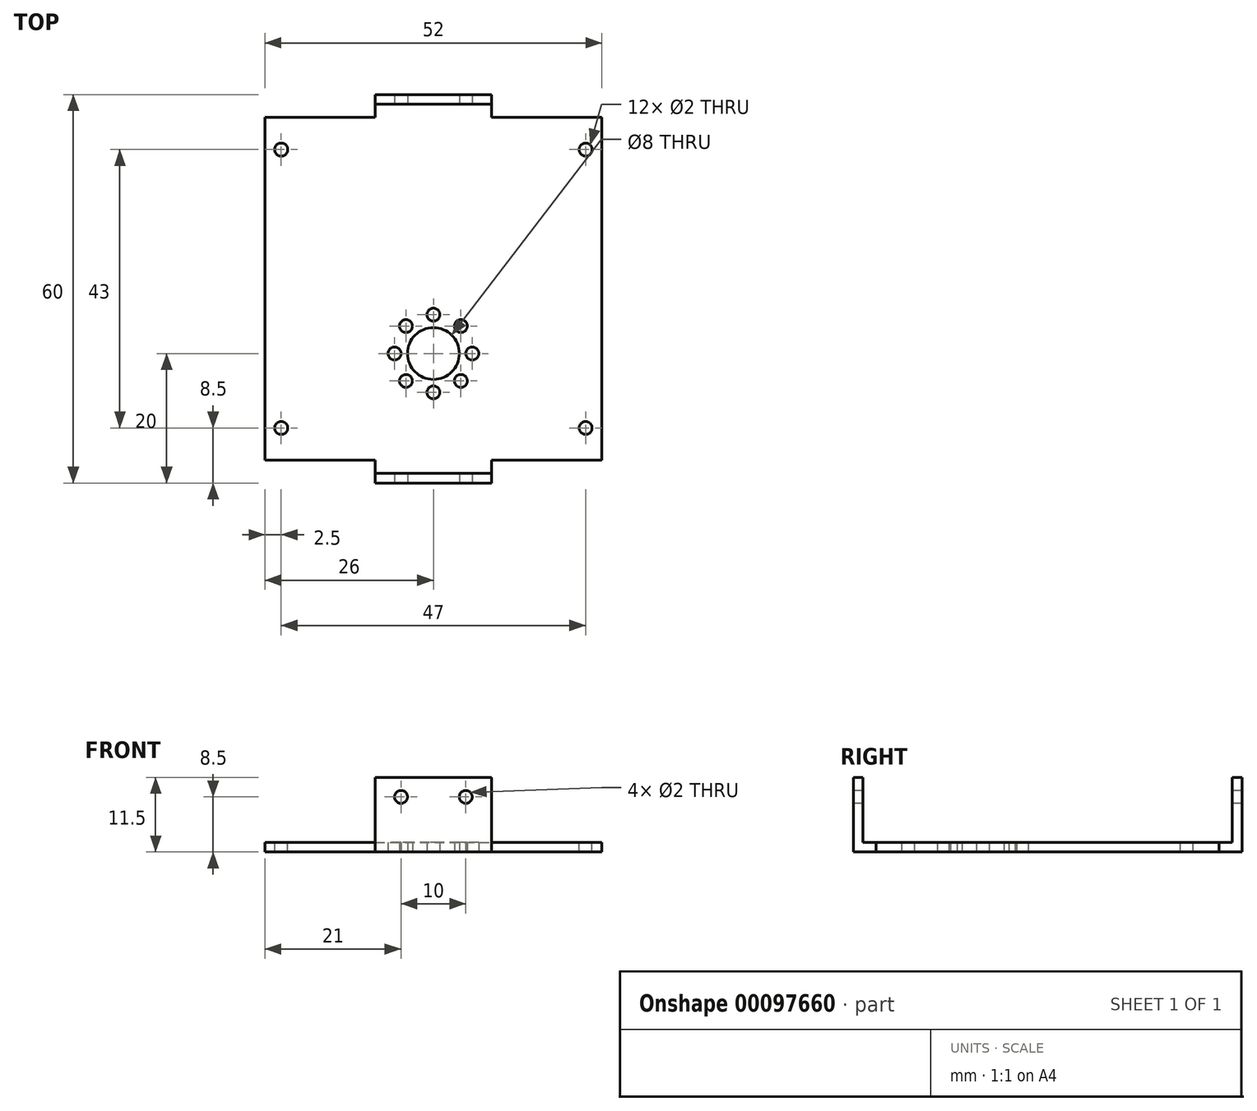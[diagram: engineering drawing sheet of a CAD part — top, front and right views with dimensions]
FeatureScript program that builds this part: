
annotation { "Feature Type Name" : "Feature", "Feature Type Description" : "" }
export const myFeature = defineFeature(function(context is Context, id is Id, definition is map)
    precondition{}
    {
        {
            var Q0;
            Q0=qCreatedBy(makeId("Top.planeOp"),FACE);
            var sketch = newSketch(context, id + "F0", { "sketchPlane" : qUnion([Q0])});
            skCircle(sketch, "E0", {"center": v(0, 0) * mm, "radius": 4 * mm});
            skCircle(sketch, "E1", {"center": v(0, 6) * mm, "radius": 1 * mm});
            skCircle(sketch, "E2.1.0", {"center": v(-4.24, 4.24) * mm, "radius": 1 * mm});
            skCircle(sketch, "E2.2.0", {"center": v(-6, 0) * mm, "radius": 1 * mm});
            skCircle(sketch, "E2.3.0", {"center": v(-4.24, -4.24) * mm, "radius": 1 * mm});
            skCircle(sketch, "E2.4.0", {"center": v(0, -6) * mm, "radius": 1 * mm});
            skCircle(sketch, "E2.5.0", {"center": v(4.24, -4.24) * mm, "radius": 1 * mm});
            skCircle(sketch, "E2.6.0", {"center": v(6, 0) * mm, "radius": 1 * mm});
            skCircle(sketch, "E2.7.0", {"center": v(4.24, 4.24) * mm, "radius": 1 * mm});
            skLineSegment(sketch, "E3.bottom", {"start": v(-9, -20) * mm, "end": v(9, -20) * mm});
            skLineSegment(sketch, "E3.top", {"start": v(-9, 40) * mm, "end": v(9, 40) * mm});
            skLineSegment(sketch, "E3.left", {"start": v(-9, -20) * mm, "end": v(-9, 40) * mm});
            skLineSegment(sketch, "E3.right", {"start": v(9, -20) * mm, "end": v(9, 40) * mm});
            skPoint(sketch, "E4", {"position": v(0, 40) * mm});
            skSolve(sketch);
        }
        {
            var Q0;
            Q0 = qSketchRegion(id + "F0", true);
            extrude(context, id + "F1", {"entities" : qUnion([Q0]), "depth" : 1.5 * mm});
        }
        {
            var Q0;
            Q0=makeQuery(id+"F1.opExtrude","CAP_FACE",FACE,{"disambiguationData":[OSD([sQuery(id+"F0.wireOp",EDGE,"E0"),sQuery(id+"F0.wireOp",EDGE,"E1"),sQuery(id+"F0.wireOp",EDGE,"E2.1.0"),sQuery(id+"F0.wireOp",EDGE,"E2.2.0"),sQuery(id+"F0.wireOp",EDGE,"E2.3.0"),sQuery(id+"F0.wireOp",EDGE,"E2.4.0"),sQuery(id+"F0.wireOp",EDGE,"E2.5.0"),sQuery(id+"F0.wireOp",EDGE,"E2.6.0"),sQuery(id+"F0.wireOp",EDGE,"E2.7.0"),sQuery(id+"F0.wireOp",EDGE,"E3.bottom"),sQuery(id+"F0.wireOp",EDGE,"E3.top"),sQuery(id+"F0.wireOp",EDGE,"E3.left"),sQuery(id+"F0.wireOp",EDGE,"E3.right")])],"isStart":false});
            var sketch = newSketch(context, id + "F2", { "sketchPlane" : qUnion([Q0])});
            skLineSegment(sketch, "E5.bottom", {"start": v(-9, 40) * mm, "end": v(9, 40) * mm});
            skLineSegment(sketch, "E5.top", {"start": v(-9, 38.5) * mm, "end": v(9, 38.5) * mm});
            skLineSegment(sketch, "E5.left", {"start": v(-9, 40) * mm, "end": v(-9, 38.5) * mm});
            skLineSegment(sketch, "E5.right", {"start": v(9, 40) * mm, "end": v(9, 38.5) * mm});
            skLineSegment(sketch, "E6.bottom", {"start": v(-9, -20) * mm, "end": v(9, -20) * mm});
            skLineSegment(sketch, "E6.top", {"start": v(-9, -18.5) * mm, "end": v(9, -18.5) * mm});
            skLineSegment(sketch, "E6.left", {"start": v(-9, -20) * mm, "end": v(-9, -18.5) * mm});
            skLineSegment(sketch, "E6.right", {"start": v(9, -20) * mm, "end": v(9, -18.5) * mm});
            skSolve(sketch);
        }
        {
            var Q0;
            Q0 = qSketchRegion(id + "F2", true);
            extrude(context, id + "F3", {"entities" : qUnion([Q0]), "operationType" : NewBodyOperationType.ADD, "depth" : 10 * mm});
        }
        {
            var Q0;
            Q0=makeQuery(id+"F3.boolean.opBoolean","MERGE",FACE,{"derivedFrom":[makeQuery(id+"F1.opExtrude","SWEPT_FACE",FACE,{"disambiguationData":[OSD([sQuery(id+"F0.wireOp",EDGE,"E3.bottom")])]}),makeQuery(id+"F3.opExtrude","SWEPT_FACE",FACE,{"disambiguationData":[OSD([sQuery(id+"F2.wireOp",EDGE,"E6.bottom")])]})]});
            var sketch = newSketch(context, id + "F4", { "sketchPlane" : qUnion([Q0])});
            skCircle(sketch, "E7", {"center": v(5, 8.5) * mm, "radius": 1 * mm});
            skCircle(sketch, "E8.MirrorC", {"center": v(-5, 8.5) * mm, "radius": 1 * mm});
            skSolve(sketch);
        }
        {
            var Q0;
            Q0 = qSketchRegion(id + "F4", true);
            extrude(context, id + "F5", {"entities" : qUnion([Q0]), "operationType" : NewBodyOperationType.REMOVE, "endBound" : BoundingType.THROUGH_ALL, "oppositeDirection" : true, "depth" : 25 * mm});
        }
        {
            var Q0;
            Q0=makeQuery(id+"F3.boolean.opBoolean","MERGE",FACE,{"derivedFrom":[makeQuery(id+"F1.opExtrude","SWEPT_FACE",FACE,{"disambiguationData":[OSD([sQuery(id+"F0.wireOp",EDGE,"E3.right")])]}),makeQuery(id+"F3.opExtrude","SWEPT_FACE",FACE,{"disambiguationData":[OSD([sQuery(id+"F2.wireOp",EDGE,"E5.right")])]}),makeQuery(id+"F3.opExtrude","SWEPT_FACE",FACE,{"disambiguationData":[OSD([sQuery(id+"F2.wireOp",EDGE,"E6.right")])]})]});
            var sketch = newSketch(context, id + "F6", { "sketchPlane" : qUnion([Q0])});
            skLineSegment(sketch, "E9.bottom", {"start": v(-16.5, 1.5) * mm, "end": v(36.5, 1.5) * mm});
            skLineSegment(sketch, "E9.top", {"start": v(-16.5, 0) * mm, "end": v(36.5, 0) * mm});
            skLineSegment(sketch, "E9.left", {"start": v(-16.5, 1.5) * mm, "end": v(-16.5, 0) * mm});
            skLineSegment(sketch, "E9.right", {"start": v(36.5, 1.5) * mm, "end": v(36.5, 0) * mm});
            skSolve(sketch);
        }
        {
            var Q0;
            Q0 = qSketchRegion(id + "F6", true);
            extrude(context, id + "F7", {"entities" : qUnion([Q0]), "operationType" : NewBodyOperationType.ADD, "depth" : 17 * mm});
        }
        {
            var Q0;
            Q0=makeQuery(id+"F7.boolean.opBoolean","MERGE",FACE,{"derivedFrom":[makeQuery(id+"F1.opExtrude","CAP_FACE",FACE,{"disambiguationData":[OSD([sQuery(id+"F0.wireOp",EDGE,"E0"),sQuery(id+"F0.wireOp",EDGE,"E1"),sQuery(id+"F0.wireOp",EDGE,"E2.1.0"),sQuery(id+"F0.wireOp",EDGE,"E2.2.0"),sQuery(id+"F0.wireOp",EDGE,"E2.3.0"),sQuery(id+"F0.wireOp",EDGE,"E2.4.0"),sQuery(id+"F0.wireOp",EDGE,"E2.5.0"),sQuery(id+"F0.wireOp",EDGE,"E2.6.0"),sQuery(id+"F0.wireOp",EDGE,"E2.7.0"),sQuery(id+"F0.wireOp",EDGE,"E3.bottom"),sQuery(id+"F0.wireOp",EDGE,"E3.top"),sQuery(id+"F0.wireOp",EDGE,"E3.left"),sQuery(id+"F0.wireOp",EDGE,"E3.right")])],"isStart":false}),makeQuery(id+"F7.opExtrude","SWEPT_FACE",FACE,{"disambiguationData":[OSD([sQuery(id+"F6.wireOp",EDGE,"E9.bottom")])]})]});
            var sketch = newSketch(context, id + "F8", { "sketchPlane" : qUnion([Q0])});
            skCircle(sketch, "E10", {"center": v(23.5, 31.5) * mm, "radius": 1 * mm});
            skLineSegment(sketch, "E11", {"start": v(26, 10) * mm, "end": v(-9, 10) * mm, "construction": true});
            skCircle(sketch, "E12.MirrorC", {"center": v(23.5, -11.5) * mm, "radius": 1 * mm});
            skSolve(sketch);
        }
        {
            var Q0;
            Q0 = qSketchRegion(id + "F8", true);
            extrude(context, id + "F9", {"entities" : qUnion([Q0]), "operationType" : NewBodyOperationType.REMOVE, "endBound" : BoundingType.UP_TO_NEXT, "oppositeDirection" : true, "depth" : 25 * mm});
        }
        {
            var Q0;
            Q0=makeQuery(id+"F1.opExtrude","SWEPT_BODY",BODY,{"disambiguationData":[OSD([sQuery(id+"F0.wireOp",EDGE,"E0"),sQuery(id+"F0.wireOp",EDGE,"E1"),sQuery(id+"F0.wireOp",EDGE,"E2.1.0"),sQuery(id+"F0.wireOp",EDGE,"E2.2.0"),sQuery(id+"F0.wireOp",EDGE,"E2.3.0"),sQuery(id+"F0.wireOp",EDGE,"E2.4.0"),sQuery(id+"F0.wireOp",EDGE,"E2.5.0"),sQuery(id+"F0.wireOp",EDGE,"E2.6.0"),sQuery(id+"F0.wireOp",EDGE,"E2.7.0"),sQuery(id+"F0.wireOp",EDGE,"E3.bottom"),sQuery(id+"F0.wireOp",EDGE,"E3.top"),sQuery(id+"F0.wireOp",EDGE,"E3.left"),sQuery(id+"F0.wireOp",EDGE,"E3.right")])]});
            var Q1;
            Q1=qCreatedBy(makeId("Right.planeOp"),FACE);
            mirror(context, id + "F10", {"operationType" : NewBodyOperationType.ADD, "entities" : qUnion([Q0]), "mirrorPlane" : qUnion([Q1])});
        }
    });
